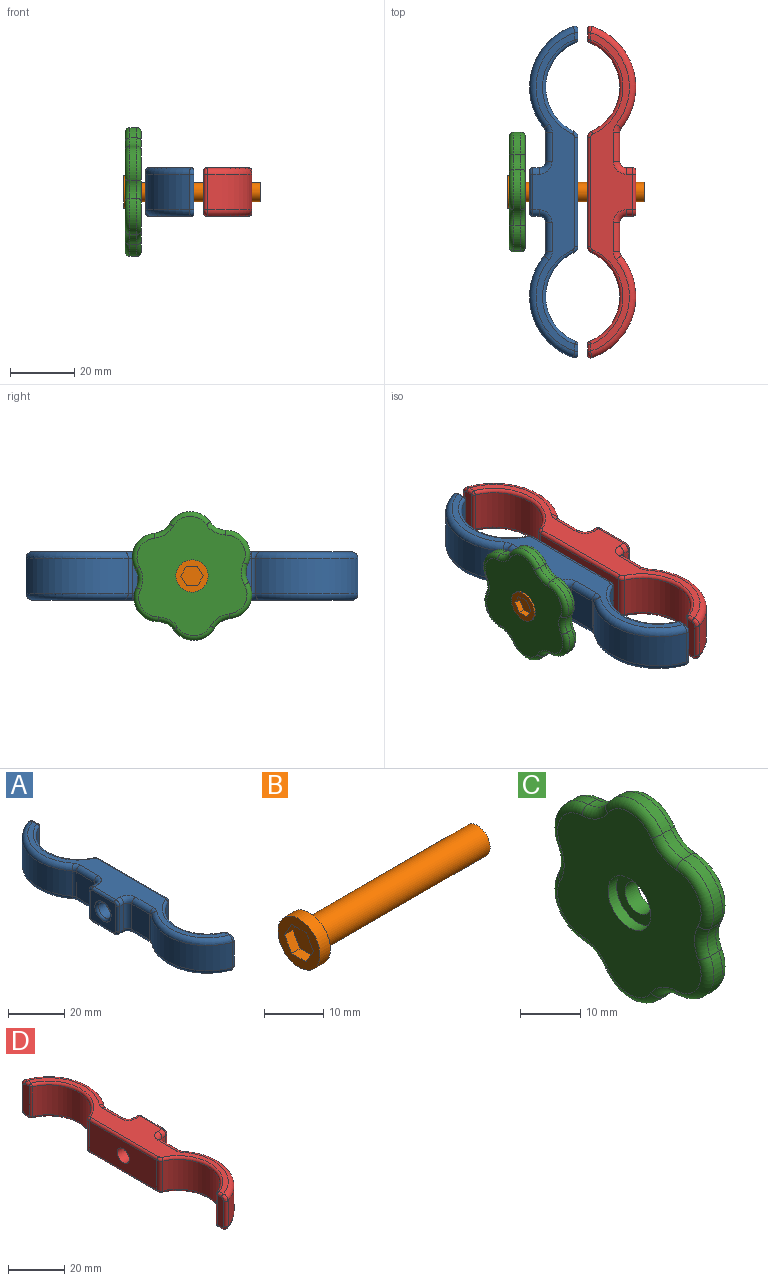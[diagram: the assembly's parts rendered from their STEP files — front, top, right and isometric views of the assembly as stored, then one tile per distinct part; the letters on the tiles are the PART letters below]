
ASSEMBLY  parts=4 mates=3
PART A: 76 faces, bbox 16.8x106.1x15.3 mm
  f0: cylinder r=15mm len=27.57mm, axis (0,0,-1), area 454.9mm2, adj f39,f51,f59,f63
  f1: plane 34.02x13mm, normal (1,0,0), area 411mm2, adj f14,f39,f40,f41,f66
  f2: cylinder r=15mm len=27.57mm, axis (0,0,-1), area 454.9mm2, adj f40,f46,f56,f62
  f3: plane 13x3.2mm, normal (1,0,0), area 41.1mm2, adj f43,f47,f48,f53,f56,f57
  f4: cylinder r=20mm len=31.67mm, axis (0,0,-1), area 426.2mm2, adj f32,f36,f38,f48
  f5: plane 11x9.04mm, normal (-1,0,0), area 99.4mm2, adj f30,f31,f35,f36
  f6: plane 11x2mm, normal (0,1,0), area 22mm2, adj f27,f29,f30,f72
  f7: plane 13x13mm, normal (-1,0,0), area 114mm2, adj f67,f68,f69,f70,f71,f72,f73,f74
  f8: plane 11x2mm, normal (0,-1,0), area 22mm2, adj f15,f19,f20,f69
  f9: plane 11x9.04mm, normal (-1,0,0), area 99.4mm2, adj f18,f19,f23,f24
  f10: cylinder r=20mm len=31.67mm, axis (0,0,-1), area 426.2mm2, adj f17,f23,f26,f49
  f11: plane 13x3.2mm, normal (1,0,0), area 41.1mm2, adj f44,f49,f50,f54,f58,f59
  f12: plane 98.94x13mm, normal (0,0,1), area 481.4mm2, adj f20,f22,f24,f25,f26,f29,f33,f35
  f13: plane 98.94x13mm, normal (0,0,-1), area 481.4mm2, adj f15,f16,f17,f18,f21,f27,f28,f31
  f14: cylinder r=3.15mm len=14mm, axis (-1,0,0), area 277.1mm2, adj f1,f75
  f15: cylinder r=2mm len=2mm, axis (1,0,0), area 6.3mm2, adj f8,f13,f16,f71
  f16: torus R=4mm, axis (0,0,1), area 13.5mm2, adj f13,f15,f18,f19
  f17: torus R=18mm, axis (0,0,1), area 116.9mm2, adj f10,f13,f21,f54
  f18: cylinder r=2mm len=9.04mm, axis (0,-1,0), area 28.4mm2, adj f9,f13,f16,f21
  f19: cylinder r=2mm len=11mm, axis (0,0,1), area 34.6mm2, adj f8,f9,f16,f22
  f20: cylinder r=2mm len=2mm, axis (-1,0,0), area 6.3mm2, adj f8,f12,f22,f67
  f21: torus R=4mm, axis (0,0,1), area 5.9mm2, adj f13,f17,f18,f23
  f22: torus R=4mm, axis (0,0,1), area 13.5mm2, adj f12,f19,f20,f24
  f23: cylinder r=2mm len=11mm, axis (0,0,-1), area 15.1mm2, adj f9,f10,f21,f25
  f24: cylinder r=2mm len=9.04mm, axis (0,1,0), area 28.4mm2, adj f9,f12,f22,f25
  f25: torus R=4mm, axis (0,0,1), area 5.9mm2, adj f12,f23,f24,f26
  f26: torus R=18mm, axis (0,0,1), area 116.9mm2, adj f10,f12,f25,f44
  f27: cylinder r=2mm len=2mm, axis (-1,0,0), area 6.3mm2, adj f6,f13,f28,f74
  f28: torus R=4mm, axis (0,0,1), area 13.5mm2, adj f13,f27,f30,f31
  f29: cylinder r=2mm len=2mm, axis (1,0,0), area 6.3mm2, adj f6,f12,f33,f70
  f30: cylinder r=2mm len=11mm, axis (0,0,-1), area 34.6mm2, adj f5,f6,f28,f33
  f31: cylinder r=2mm len=9.04mm, axis (0,-1,0), area 28.4mm2, adj f5,f13,f28,f34
  f32: torus R=18mm, axis (0,0,1), area 116.9mm2, adj f4,f13,f34,f53
  f33: torus R=4mm, axis (0,0,1), area 13.5mm2, adj f12,f29,f30,f35
  f34: torus R=4mm, axis (0,0,1), area 5.9mm2, adj f13,f31,f32,f36
  f35: cylinder r=2mm len=9.04mm, axis (0,1,0), area 28.4mm2, adj f5,f12,f33,f37
  f36: cylinder r=2mm len=11mm, axis (0,0,-1), area 15.1mm2, adj f4,f5,f34,f37
  f37: torus R=4mm, axis (0,0,1), area 5.9mm2, adj f12,f35,f36,f38
  f38: torus R=18mm, axis (0,0,1), area 116.9mm2, adj f4,f12,f37,f43
  f39: cylinder r=2mm len=13mm, axis (0,0,-1), area 29.8mm2, adj f0,f1,f45,f65
  f40: cylinder r=2mm len=13mm, axis (0,0,-1), area 29.8mm2, adj f1,f2,f42,f64
  f41: cylinder r=1mm len=34.02mm, axis (0,-1,0), area 53.4mm2, adj f1,f12,f42,f45
  f42: torus R=1mm, axis (0,0,1), area 2.9mm2, adj f12,f40,f41,f46
  f43: bspline ~2.56x2.56mm, area 4.8mm2, adj f3,f38,f47,f48
  f44: bspline ~2.91x2.56mm, area 4.8mm2, adj f11,f26,f49,f50
  f45: torus R=1mm, axis (0,0,1), area 2.9mm2, adj f12,f39,f41,f51
  f46: torus R=16mm, axis (0,0,1), area 56.3mm2, adj f2,f12,f42,f52
  f47: cylinder r=1mm len=2.14mm, axis (0,-1,0), area 3.4mm2, adj f3,f12,f43,f52
  f48: cylinder r=1mm len=11mm, axis (0,0,-1), area 20.8mm2, adj f3,f4,f43,f53
  f49: cylinder r=1mm len=11mm, axis (0,0,-1), area 20.8mm2, adj f10,f11,f44,f54
  f50: cylinder r=1mm len=2.14mm, axis (0,-1,0), area 3.4mm2, adj f11,f12,f44,f55
  f51: torus R=16mm, axis (0,0,1), area 56.3mm2, adj f0,f12,f45,f55
  f52: sphere r=1mm, area 1.2mm2, adj f46,f47,f56
  f53: bspline ~2.56x2.56mm, area 4.8mm2, adj f3,f32,f48,f57
  f54: bspline ~2.56x2.56mm, area 4.8mm2, adj f11,f17,f49,f58
  f55: sphere r=1mm, area 1.2mm2, adj f50,f51,f59
  f56: cylinder r=1mm len=13mm, axis (0,0,-1), area 15.4mm2, adj f2,f3,f52,f60
  f57: cylinder r=1mm len=2.14mm, axis (0,1,0), area 3.4mm2, adj f3,f13,f53,f60
  f58: cylinder r=1mm len=2.14mm, axis (0,1,0), area 3.4mm2, adj f11,f13,f54,f61
  f59: cylinder r=1mm len=13mm, axis (0,0,-1), area 15.4mm2, adj f0,f11,f55,f61
  f60: sphere r=1mm, area 1.2mm2, adj f56,f57,f62
  f61: sphere r=1mm, area 1.2mm2, adj f58,f59,f63
  f62: torus R=16mm, axis (0,0,1), area 56.3mm2, adj f2,f13,f60,f64
  f63: torus R=16mm, axis (0,0,1), area 56.3mm2, adj f0,f13,f61,f65
  f64: torus R=1mm, axis (0,0,1), area 2.9mm2, adj f13,f40,f62,f66
  f65: torus R=1mm, axis (0,0,1), area 2.9mm2, adj f13,f39,f63,f66
  f66: cylinder r=1mm len=34.02mm, axis (0,1,0), area 53.4mm2, adj f1,f13,f64,f65
  f67: torus R=1mm, axis (1,0,0), area 4mm2, adj f7,f20,f68,f69
  f68: cylinder r=1mm len=11mm, axis (0,1,0), area 17.3mm2, adj f7,f12,f67,f70
  f69: cylinder r=1mm len=11mm, axis (0,0,1), area 17.3mm2, adj f7,f8,f67,f71
  f70: torus R=1mm, axis (1,0,0), area 4mm2, adj f7,f29,f68,f72
  f71: torus R=1mm, axis (1,0,0), area 4mm2, adj f7,f15,f69,f73
  f72: cylinder r=1mm len=11mm, axis (0,0,-1), area 17.3mm2, adj f6,f7,f70,f74
  f73: cylinder r=1mm len=11mm, axis (0,-1,0), area 17.3mm2, adj f7,f13,f71,f74
  f74: torus R=1mm, axis (1,0,0), area 4mm2, adj f7,f27,f72,f73
  f75: torus R=4.15mm, axis (1,0,0), area 34.7mm2, adj f7,f14
PART B: 12 faces, bbox 42.5x10x10 mm
  f0: plane 10x10mm, normal (-1,0,0), area 47.4mm2, adj f1,f3,f4,f5,f6,f7,f8
  f1: cylinder r=5mm len=10mm, axis (-1,0,0), area 78.5mm2, adj f0,f2
  f2: plane 10x10mm, normal (1,0,0), area 50.3mm2, adj f1,f10
  f3: plane 3x2mm, normal (0,-0.87,-0.5), area 6.9mm2, adj f0,f4,f8,f9
  f4: plane 3x2mm, normal (0,-0.87,0.5), area 6.9mm2, adj f0,f3,f5,f9
  f5: plane 3.46x2mm, normal (0,0,1), area 6.9mm2, adj f0,f4,f6,f9
  f6: plane 3x2mm, normal (0,0.87,0.5), area 6.9mm2, adj f0,f5,f7,f9
  f7: plane 3x2mm, normal (0,0.87,-0.5), area 6.9mm2, adj f0,f6,f8,f9
  f8: plane 3.46x2mm, normal (0,0,-1), area 6.9mm2, adj f0,f3,f7,f9
  f9: plane 6.93x6mm, normal (-1,0,0), area 31.2mm2, adj f3,f4,f5,f6,f7,f8
  f10: cylinder r=3mm len=40mm, axis (-1,0,0), area 754mm2, adj f2,f11
  f11: plane 6x6mm, normal (1,0,0), area 28.3mm2, adj f10
PART C: 41 faces, bbox 5x37.9x41.2 mm
  f0: cylinder r=3mm len=6mm, axis (1,0,0), area 56.5mm2, adj f8,f16
  f1: cylinder r=7.5mm len=12.66mm, axis (1,0,0), area 30.1mm2, adj f9,f10,f19,f29
  f2: cylinder r=7.5mm len=10.97mm, axis (1,0,0), area 30.1mm2, adj f10,f11,f23,f32
  f3: cylinder r=7.5mm len=10.97mm, axis (1,0,0), area 30.1mm2, adj f11,f13,f27,f36
  f4: cylinder r=7.5mm len=12.66mm, axis (1,0,0), area 30.1mm2, adj f13,f14,f26,f40
  f5: cylinder r=7.5mm len=10.97mm, axis (1,0,0), area 30.1mm2, adj f12,f14,f22,f37
  f6: cylinder r=7.5mm len=10.97mm, axis (1,0,0), area 30.1mm2, adj f9,f12,f18,f33
  f7: plane 37x33.65mm, normal (-1,0,0), area 830.8mm2, adj f15,f29,f30,f31,f32,f33,f34,f35
  f8: plane 37x33.65mm, normal (1,0,0), area 881mm2, adj f0,f17,f18,f19,f20,f21,f22,f23
  f9: cylinder r=6mm len=4.81mm, axis (-1,0,0), area 11.6mm2, adj f1,f6,f17,f31
  f10: cylinder r=6mm len=4.81mm, axis (-1,0,0), area 11.6mm2, adj f1,f2,f21,f30
  f11: cylinder r=6mm len=5.56mm, axis (-1,0,0), area 11.6mm2, adj f2,f3,f25,f34
  f12: cylinder r=6mm len=5.56mm, axis (-1,0,0), area 11.6mm2, adj f5,f6,f20,f35
  f13: cylinder r=6mm len=4.81mm, axis (-1,0,0), area 11.6mm2, adj f3,f4,f28,f38
  f14: cylinder r=6mm len=4.81mm, axis (-1,0,0), area 11.6mm2, adj f4,f5,f24,f39
  f15: cylinder r=5mm len=10mm, axis (-1,0,0), area 62.8mm2, adj f7,f16
  f16: plane 10x10mm, normal (-1,0,0), area 50.3mm2, adj f0,f15
  f17: torus R=7.5mm, axis (-1,0,0), area 14.8mm2, adj f8,f9,f18,f19
  f18: torus R=6mm, axis (-1,0,0), area 32.9mm2, adj f6,f8,f17,f20
  f19: torus R=6mm, axis (-1,0,0), area 32.9mm2, adj f1,f8,f17,f21
  f20: torus R=7.5mm, axis (-1,0,0), area 14.8mm2, adj f8,f12,f18,f22
  f21: torus R=7.5mm, axis (-1,0,0), area 14.8mm2, adj f8,f10,f19,f23
  f22: torus R=6mm, axis (-1,0,0), area 32.9mm2, adj f5,f8,f20,f24
  f23: torus R=6mm, axis (-1,0,0), area 32.9mm2, adj f2,f8,f21,f25
  f24: torus R=7.5mm, axis (-1,0,0), area 14.8mm2, adj f8,f14,f22,f26
  f25: torus R=7.5mm, axis (-1,0,0), area 14.8mm2, adj f8,f11,f23,f27
  f26: torus R=6mm, axis (-1,0,0), area 32.9mm2, adj f4,f8,f24,f28
  f27: torus R=6mm, axis (-1,0,0), area 32.9mm2, adj f3,f8,f25,f28
  f28: torus R=7.5mm, axis (-1,0,0), area 14.8mm2, adj f8,f13,f26,f27
  f29: torus R=6mm, axis (-1,0,0), area 32.9mm2, adj f1,f7,f30,f31
  f30: torus R=7.5mm, axis (-1,0,0), area 14.8mm2, adj f7,f10,f29,f32
  f31: torus R=7.5mm, axis (-1,0,0), area 14.8mm2, adj f7,f9,f29,f33
  f32: torus R=6mm, axis (-1,0,0), area 32.9mm2, adj f2,f7,f30,f34
  f33: torus R=6mm, axis (-1,0,0), area 32.9mm2, adj f6,f7,f31,f35
  f34: torus R=7.5mm, axis (-1,0,0), area 14.8mm2, adj f7,f11,f32,f36
  f35: torus R=7.5mm, axis (-1,0,0), area 14.8mm2, adj f7,f12,f33,f37
  f36: torus R=6mm, axis (-1,0,0), area 32.9mm2, adj f3,f7,f34,f38
  f37: torus R=6mm, axis (-1,0,0), area 32.9mm2, adj f5,f7,f35,f39
  f38: torus R=7.5mm, axis (-1,0,0), area 14.8mm2, adj f7,f13,f36,f40
  f39: torus R=7.5mm, axis (-1,0,0), area 14.8mm2, adj f7,f14,f37,f40
  f40: torus R=6mm, axis (-1,0,0), area 32.9mm2, adj f4,f7,f38,f39
PART D: 89 faces, bbox 16.8x106.1x15.3 mm
  f0: plane 13x5.76mm, normal (1,0,0), area 22mm2, adj f75,f80,f81,f84,f85,f86,f87,f88
  f1: plane 13x5.76mm, normal (1,0,0), area 22mm2, adj f76,f77,f78,f79,f81,f82,f83,f86
  f2: cylinder r=3mm len=10mm, axis (-1,0,0), area 188.5mm2, adj f8,f22
  f3: plane 11x2mm, normal (0,1,0), area 22mm2, adj f23,f27,f28,f81
  f4: plane 11x9.04mm, normal (1,0,0), area 99.4mm2, adj f26,f27,f31,f32
  f5: cylinder r=20mm len=31.67mm, axis (0,0,-1), area 426.2mm2, adj f25,f31,f34,f54
  f6: plane 13x3.2mm, normal (-1,0,0), area 41.1mm2, adj f50,f54,f55,f60,f64,f65
  f7: cylinder r=15mm len=27.57mm, axis (0,0,-1), area 454.9mm2, adj f47,f56,f65,f70
  f8: plane 34.02x13mm, normal (-1,0,0), area 413.9mm2, adj f2,f47,f48,f49,f74
  f9: cylinder r=15mm len=27.57mm, axis (0,0,-1), area 454.9mm2, adj f48,f57,f66,f71
  f10: plane 13x3.2mm, normal (-1,0,0), area 41.1mm2, adj f53,f58,f59,f63,f66,f67
  f11: cylinder r=20mm len=31.67mm, axis (0,0,-1), area 426.2mm2, adj f40,f44,f46,f59
  f12: plane 11x9.04mm, normal (1,0,0), area 99.4mm2, adj f38,f39,f43,f44
  f13: plane 11x2mm, normal (0,-1,0), area 22mm2, adj f35,f37,f38,f86
  f14: plane 98.94x13mm, normal (0,0,1), area 481.4mm2, adj f28,f30,f32,f33,f34,f37,f41,f43
  f15: plane 98.94x13mm, normal (0,0,-1), area 481.4mm2, adj f23,f24,f25,f26,f29,f35,f36,f39
  f16: plane 5x4mm, normal (0,0.87,-0.5), area 23.1mm2, adj f17,f21,f22,f83
  f17: plane 5x4mm, normal (0,0.87,0.5), area 23.1mm2, adj f16,f18,f22,f84
  f18: plane 5.77x4mm, normal (0,0,1), area 23.1mm2, adj f17,f19,f22,f80
  f19: plane 5x4mm, normal (0,-0.87,0.5), area 23.1mm2, adj f18,f20,f22,f75
  f20: plane 5x4mm, normal (0,-0.87,-0.5), area 23.1mm2, adj f19,f21,f22,f76
  f21: plane 5.77x4mm, normal (0,0,-1), area 23.1mm2, adj f16,f20,f22,f79
  f22: plane 11.55x10mm, normal (1,0,0), area 58.3mm2, adj f2,f16,f17,f18,f19,f20,f21
  f23: cylinder r=2mm len=2mm, axis (-1,0,0), area 6.3mm2, adj f3,f15,f24,f85
  f24: torus R=4mm, axis (0,0,1), area 13.5mm2, adj f15,f23,f26,f27
  f25: torus R=18mm, axis (0,0,1), area 116.9mm2, adj f5,f15,f29,f60
  f26: cylinder r=2mm len=9.04mm, axis (0,1,0), area 28.4mm2, adj f4,f15,f24,f29
  f27: cylinder r=2mm len=11mm, axis (0,0,-1), area 34.6mm2, adj f3,f4,f24,f30
  f28: cylinder r=2mm len=2mm, axis (1,0,0), area 6.3mm2, adj f3,f14,f30,f77
  f29: torus R=4mm, axis (0,0,1), area 5.9mm2, adj f15,f25,f26,f31
  f30: torus R=4mm, axis (0,0,1), area 13.5mm2, adj f14,f27,f28,f32
  f31: cylinder r=2mm len=11mm, axis (0,0,-1), area 15.1mm2, adj f4,f5,f29,f33
  f32: cylinder r=2mm len=9.04mm, axis (0,-1,0), area 28.4mm2, adj f4,f14,f30,f33
  f33: torus R=4mm, axis (0,0,1), area 5.9mm2, adj f14,f31,f32,f34
  f34: torus R=18mm, axis (0,0,1), area 116.9mm2, adj f5,f14,f33,f50
  f35: cylinder r=2mm len=2mm, axis (1,0,0), area 6.3mm2, adj f13,f15,f36,f88
  f36: torus R=4mm, axis (0,0,1), area 13.5mm2, adj f15,f35,f38,f39
  f37: cylinder r=2mm len=2mm, axis (-1,0,0), area 6.3mm2, adj f13,f14,f41,f82
  f38: cylinder r=2mm len=11mm, axis (0,0,1), area 34.6mm2, adj f12,f13,f36,f41
  f39: cylinder r=2mm len=9.04mm, axis (0,1,0), area 28.4mm2, adj f12,f15,f36,f42
  f40: torus R=18mm, axis (0,0,1), area 116.9mm2, adj f11,f15,f42,f63
  f41: torus R=4mm, axis (0,0,1), area 13.5mm2, adj f14,f37,f38,f43
  f42: torus R=4mm, axis (0,0,1), area 5.9mm2, adj f15,f39,f40,f44
  f43: cylinder r=2mm len=9.04mm, axis (0,-1,0), area 28.4mm2, adj f12,f14,f41,f45
  f44: cylinder r=2mm len=11mm, axis (0,0,-1), area 15.1mm2, adj f11,f12,f42,f45
  f45: torus R=4mm, axis (0,0,1), area 5.9mm2, adj f14,f43,f44,f46
  f46: torus R=18mm, axis (0,0,1), area 116.9mm2, adj f11,f14,f45,f53
  f47: cylinder r=2mm len=13mm, axis (0,0,-1), area 29.8mm2, adj f7,f8,f51,f72
  f48: cylinder r=2mm len=13mm, axis (0,0,-1), area 29.8mm2, adj f8,f9,f52,f73
  f49: cylinder r=1mm len=34.02mm, axis (0,1,0), area 53.4mm2, adj f8,f14,f51,f52
  f50: bspline ~2.91x2.56mm, area 4.8mm2, adj f6,f34,f54,f55
  f51: torus R=1mm, axis (0,0,1), area 2.9mm2, adj f14,f47,f49,f56
  f52: torus R=1mm, axis (0,0,1), area 2.9mm2, adj f14,f48,f49,f57
  f53: bspline ~2.56x2.56mm, area 4.8mm2, adj f10,f46,f58,f59
  f54: cylinder r=1mm len=11mm, axis (0,0,-1), area 20.8mm2, adj f5,f6,f50,f60
  f55: cylinder r=1mm len=2.14mm, axis (0,1,0), area 3.4mm2, adj f6,f14,f50,f61
  f56: torus R=16mm, axis (0,0,1), area 56.3mm2, adj f7,f14,f51,f61
  f57: torus R=16mm, axis (0,0,1), area 56.3mm2, adj f9,f14,f52,f62
  f58: cylinder r=1mm len=2.14mm, axis (0,1,0), area 3.4mm2, adj f10,f14,f53,f62
  f59: cylinder r=1mm len=11mm, axis (0,0,-1), area 20.8mm2, adj f10,f11,f53,f63
  f60: bspline ~2.91x2.56mm, area 4.8mm2, adj f6,f25,f54,f64
  f61: sphere r=1mm, area 1.2mm2, adj f55,f56,f65
  f62: sphere r=1mm, area 1.2mm2, adj f57,f58,f66
  f63: bspline ~2.91x2.56mm, area 4.8mm2, adj f10,f40,f59,f67
  f64: cylinder r=1mm len=2.14mm, axis (0,-1,0), area 3.4mm2, adj f6,f15,f60,f68
  f65: cylinder r=1mm len=13mm, axis (0,0,-1), area 15.4mm2, adj f6,f7,f61,f68
  f66: cylinder r=1mm len=13mm, axis (0,0,-1), area 15.4mm2, adj f9,f10,f62,f69
  f67: cylinder r=1mm len=2.14mm, axis (0,-1,0), area 3.4mm2, adj f10,f15,f63,f69
  f68: sphere r=1mm, area 1.2mm2, adj f64,f65,f70
  f69: sphere r=1mm, area 1.2mm2, adj f66,f67,f71
  f70: torus R=16mm, axis (0,0,1), area 56.3mm2, adj f7,f15,f68,f72
  f71: torus R=16mm, axis (0,0,1), area 56.3mm2, adj f9,f15,f69,f73
  f72: torus R=1mm, axis (0,0,1), area 2.9mm2, adj f15,f47,f70,f74
  f73: torus R=1mm, axis (0,0,1), area 2.9mm2, adj f15,f48,f71,f74
  f74: cylinder r=1mm len=34.02mm, axis (0,-1,0), area 53.4mm2, adj f8,f15,f72,f73
  f75: cylinder r=1mm len=6.4mm, axis (0,-0.5,-0.87), area 9.6mm2, adj f0,f19,f76,f80,f81
  f76: cylinder r=1mm len=6.4mm, axis (0,0.5,-0.87), area 9.6mm2, adj f1,f20,f75,f79,f81
  f77: torus R=1mm, axis (1,0,0), area 4mm2, adj f1,f28,f78,f81
  f78: cylinder r=1mm len=11mm, axis (0,-1,0), area 17.3mm2, adj f1,f14,f77,f82
  f79: cylinder r=1mm len=6.93mm, axis (0,1,0), area 9.7mm2, adj f1,f21,f76,f83
  f80: cylinder r=1mm len=6.93mm, axis (0,-1,0), area 9.7mm2, adj f0,f18,f75,f84
  f81: cylinder r=1mm len=11mm, axis (0,0,1), area 17.1mm2, adj f0,f1,f3,f75,f76,f77,f85
  f82: torus R=1mm, axis (1,0,0), area 4mm2, adj f1,f37,f78,f86
  f83: cylinder r=1mm len=6.4mm, axis (0,0.5,0.87), area 9.6mm2, adj f1,f16,f79,f84,f86
  f84: cylinder r=1mm len=6.4mm, axis (0,-0.5,0.87), area 9.6mm2, adj f0,f17,f80,f83,f86
  f85: torus R=1mm, axis (1,0,0), area 4mm2, adj f0,f23,f81,f87
  f86: cylinder r=1mm len=11mm, axis (0,0,-1), area 17.1mm2, adj f0,f1,f13,f82,f83,f84,f88
  f87: cylinder r=1mm len=11mm, axis (0,1,0), area 17.3mm2, adj f0,f15,f85,f88
  f88: torus R=1mm, axis (1,0,0), area 4mm2, adj f0,f35,f86,f87
PLACE A rot(axis=(-1,0,0),179.9deg) t=(-24.25,-12.33,-13.53)mm
PLACE B rot(axis=(1,0,0),177.5deg) t=(-23.07,-12.33,-13.53)mm
PLACE C rot(axis=(1,0,0),177.5deg) t=(-22.57,-12.33,-13.53)mm
PLACE D t=(-31.25,-12.33,-13.53)mm fixed
MATE cylindrical D.f2 <-> B.f1  axis (-1,0,0) through (-21.25,-12.33,-13.53)mm
MATE cylindrical A.f75 <-> B.f10  axis (-1,0,0) through (-36.25,-12.33,-13.53)mm
MATE fastened B.f1 <-> C.f15  axis (1,0,0) through (-48.57,-12.33,-13.53)mm
